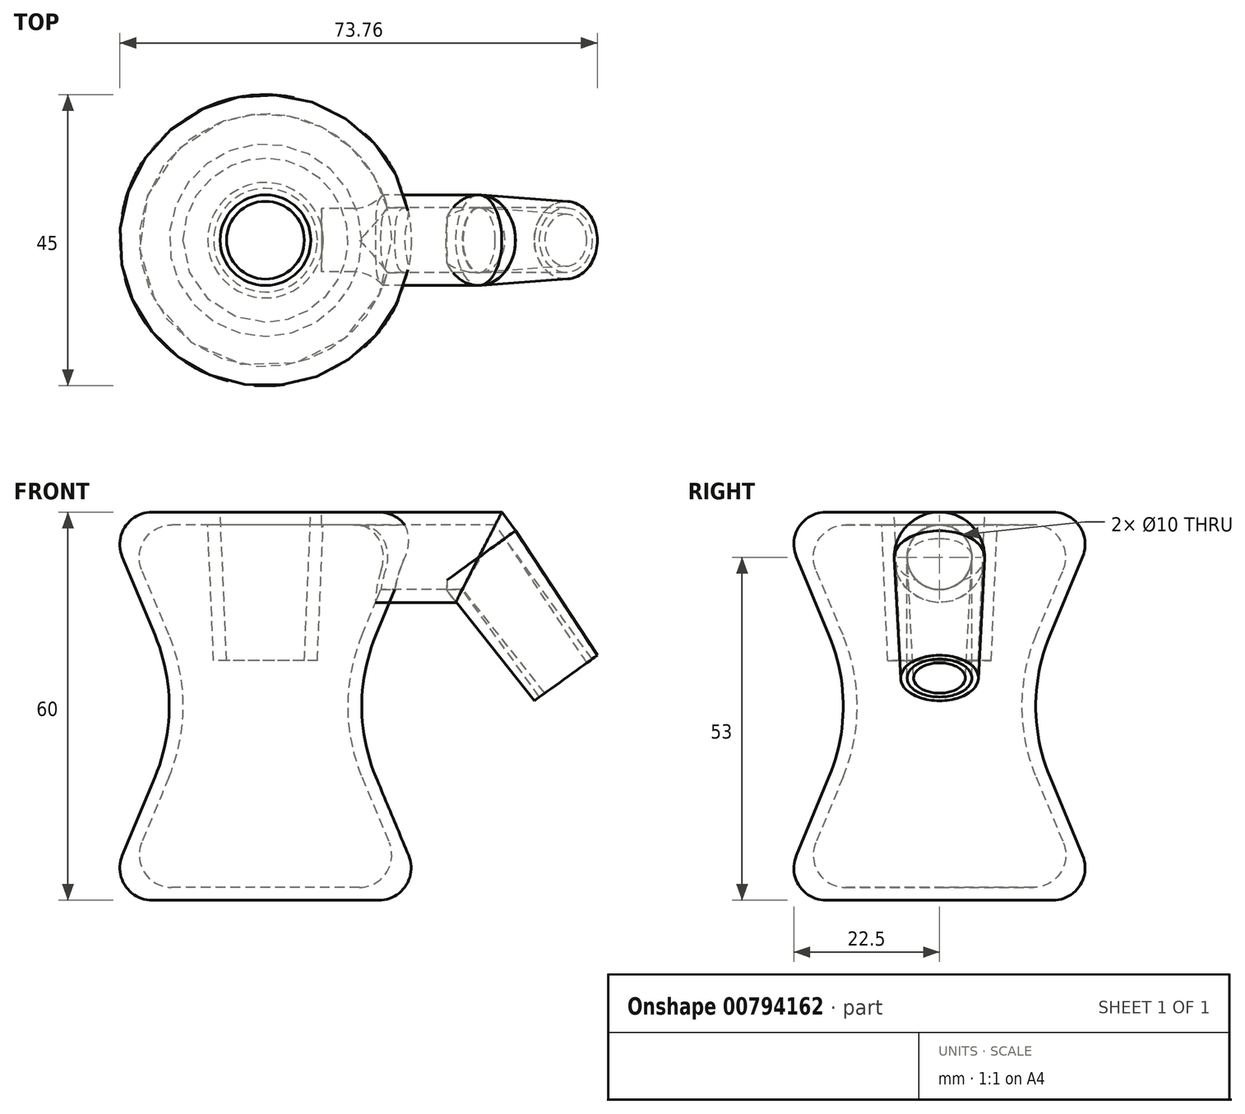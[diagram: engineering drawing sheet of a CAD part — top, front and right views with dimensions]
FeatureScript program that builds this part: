
annotation { "Feature Type Name" : "Feature", "Feature Type Description" : "" }
export const myFeature = defineFeature(function(context is Context, id is Id, definition is map)
    precondition{}
    {
        {
            var Q0;
            Q0=qCreatedBy(makeId("Front.planeOp"),FACE);
            var sketch = newSketch(context, id + "F0", { "sketchPlane" : qUnion([Q0])});
            skLineSegment(sketch, "E0", {"start": v(0, 0) * mm, "end": v(25, 0) * mm});
            skLineSegment(sketch, "E1", {"start": v(25, 0) * mm, "end": v(12.5, 30) * mm});
            skLineSegment(sketch, "E2", {"start": v(12.5, 30) * mm, "end": v(0, 30) * mm});
            skLineSegment(sketch, "E3.MirrorCS", {"start": v(25, 60) * mm, "end": v(12.5, 30) * mm});
            skLineSegment(sketch, "E4.MirrorCS", {"start": v(0, 60) * mm, "end": v(25, 60) * mm});
            skLineSegment(sketch, "E5.0", {"start": v(0, 58) * mm, "end": v(22, 58) * mm});
            skLineSegment(sketch, "E5.1", {"start": v(22, 58) * mm, "end": v(10.33, 30) * mm});
            skLineSegment(sketch, "E5.2", {"start": v(22, 2) * mm, "end": v(10.33, 30) * mm});
            skLineSegment(sketch, "E5.3", {"start": v(0, 2) * mm, "end": v(22, 2) * mm});
            skLineSegment(sketch, "E6", {"start": v(7, 60) * mm, "end": v(6, 37.02) * mm});
            skLineSegment(sketch, "E7", {"start": v(6, 37.02) * mm, "end": v(0, 37.02) * mm});
            skLineSegment(sketch, "E8", {"start": v(9, 60) * mm, "end": v(8, 37.02) * mm});
            skLineSegment(sketch, "E9", {"start": v(6, 37.02) * mm, "end": v(8, 37.02) * mm});
            skLineSegment(sketch, "E10", {"start": v(0, 60) * mm, "end": v(0, 0) * mm});
            skLineSegment(sketch, "E11", {"start": v(8.7, 53) * mm, "end": v(32.94, 53) * mm});
            skLineSegment(sketch, "E12", {"start": v(32.94, 53) * mm, "end": v(46.4, 34.35) * mm});
            skLineSegment(sketch, "E13", {"start": v(32.94, 53) * mm, "end": v(38.61, 57.1) * mm});
            skLineSegment(sketch, "E14", {"start": v(46.4, 34.35) * mm, "end": v(51.26, 37.86) * mm});
            skLineSegment(sketch, "E15", {"start": v(51.26, 37.86) * mm, "end": v(38.61, 57.1) * mm});
            skLineSegment(sketch, "E16", {"start": v(37, 55.92) * mm, "end": v(49.64, 36.69) * mm});
            skLineSegment(sketch, "E17", {"start": v(38.61, 57.1) * mm, "end": v(36.52, 60) * mm});
            skLineSegment(sketch, "E18", {"start": v(37, 55.92) * mm, "end": v(34.31, 60) * mm});
            skLineSegment(sketch, "E19", {"start": v(36.52, 60) * mm, "end": v(25, 60) * mm});
            skLineSegment(sketch, "E20", {"start": v(22, 58) * mm, "end": v(37.96, 58) * mm});
            skLineSegment(sketch, "E21", {"start": v(38.61, 57.1) * mm, "end": v(47.49, 63.5) * mm});
            skLineSegment(sketch, "E22", {"start": v(47.49, 63.5) * mm, "end": v(62.15, 37) * mm});
            skLineSegment(sketch, "E23", {"start": v(62.15, 37) * mm, "end": v(51.26, 37.86) * mm});
            skLineSegment(sketch, "E24", {"start": v(38.61, 57.1) * mm, "end": v(52.57, 37.76) * mm});
            skSolve(sketch);
        }
        {
            var Q0;
            {var subQ3=sQuery(id+"F0.wireOp",EDGE,"E0");Q0=makeQuery(id+"F0.imprint","IMPRINT",FACE,{"disambiguationData":[TD([[makeQuery(id+"F0.imprint","IMPRINT",EDGE,{"derivedFrom":subQ3}),1.0]])]});}
            var Q1;
            {var subQ0=sQuery(id+"F0.wireOp",EDGE,"EiZz0BkX-OVOf-3Axu-Wc4k-g7Euzk9zG0Uk");var subQ3=sQuery(id+"F0.wireOp",EDGE,"E5.1");var subQ5=makeQuery(id+"F0.imprint","INTERSECT",VERTEX,{"derivedFrom":[subQ3,subQ0]});Q1=makeQuery(id+"F0.imprint","IMPRINT",FACE,{"disambiguationData":[TD([[makeQuery(id+"F0.imprint","IMPRINT",EDGE,{"disambiguationData":[TD([[subQ5,-1.0]])],"derivedFrom":subQ3}),1.0]])]});}
            var Q2;
            {var subQ8=sQuery(id+"F0.wireOp",EDGE,"E3.MirrorCS");Q2=makeQuery(id+"F0.imprint","IMPRINT",FACE,{"disambiguationData":[TD([[makeQuery(id+"F0.imprint","IMPRINT",EDGE,{"derivedFrom":subQ8}),-1.0]])]});}
            var Q3;
            {var subQ0=sQuery(id+"F0.wireOp",EDGE,"E8");var subQ1=sQuery(id+"F0.wireOp",EDGE,"E4.MirrorCS");var subQ2=makeQuery(id+"F0.imprint","INTERSECT",VERTEX,{"derivedFrom":[subQ1,subQ0]});Q3=makeQuery(id+"F0.imprint","IMPRINT",FACE,{"disambiguationData":[TD([[makeQuery(id+"F0.imprint","IMPRINT",EDGE,{"disambiguationData":[TD([[subQ2,-1.0]])],"derivedFrom":subQ0}),1.0]])]});}
            var Q4;
            {var subQ0=sQuery(id+"F0.wireOp",EDGE,"E6");var subQ1=sQuery(id+"F0.wireOp",EDGE,"E4.MirrorCS");var subQ2=makeQuery(id+"F0.imprint","INTERSECT",VERTEX,{"derivedFrom":[subQ1,subQ0]});Q4=makeQuery(id+"F0.imprint","IMPRINT",FACE,{"disambiguationData":[TD([[makeQuery(id+"F0.imprint","IMPRINT",EDGE,{"disambiguationData":[TD([[subQ2,-1.0]])],"derivedFrom":subQ1}),-1.0]])]});}
            var Q5;
            {var subQ0=sQuery(id+"F0.wireOp",EDGE,"E9");Q5=makeQuery(id+"F0.imprint","IMPRINT",FACE,{"disambiguationData":[TD([[makeQuery(id+"F0.imprint","IMPRINT",EDGE,{"derivedFrom":subQ0}),1.0]])]});}
            var Q6;
            Q6=sQuery(id+"F0.wireOp",EDGE,"E10");
            revolve(context, id + "F1", {"surfaceOperationType" : NewSurfaceOperationType.NEW, "entities" : qUnion([Q0, Q1, Q2, Q3, Q4, Q5]), "axis" : qUnion([Q6]), "revolveType" : RevolveType.FULL});
        }
        {
            var Q0;
            {var subQ0=sQuery(id+"F0.wireOp",EDGE,"E15");Q0=makeQuery(id+"F0.imprint","IMPRINT",FACE,{"disambiguationData":[TD([[makeQuery(id+"F0.imprint","IMPRINT",EDGE,{"derivedFrom":subQ0}),1.0]])]});}
            var Q1;
            Q1=sQuery(id+"F0.wireOp",EDGE,"E12");
            revolve(context, id + "F2", {"surfaceOperationType" : NewSurfaceOperationType.NEW, "entities" : qUnion([Q0]), "axis" : qUnion([Q1]), "revolveType" : RevolveType.FULL});
        }
        {
            var Q0;
            Q0=sQuery(id+"F0.wireOp",VERTEX,"E12.start");
            var Q1;
            Q1=sQuery(id+"F0.wireOp",EDGE,"E11");
            cPlane(context, id + "F3", {"entities" : qUnion([Q0, Q1]), "cplaneType" : CPlaneType.CURVE_POINT, "offset" : 25 * mm, "width" : 150 * mm, "height" : 150 * mm});
        }
        {
            var Q0;
            Q0=qCreatedBy(id+"F3.planeOp",FACE);
            var sketch = newSketch(context, id + "F4", { "sketchPlane" : qUnion([Q0])});
            skPoint(sketch, "E25.0", {"position": v(0, 53) * mm});
            skCircle(sketch, "E26", {"center": v(0, 53) * mm, "radius": 7 * mm});
            skCircle(sketch, "E27", {"center": v(0, 53) * mm, "radius": 5 * mm});
            skSolve(sketch);
        }
        {
            var Q0;
            Q0=makeQuery(id+"F4.imprint","IMPRINT",FACE,{"disambiguationData":[TD([[makeQuery(id+"F4.imprint","IMPRINT",EDGE,{"derivedFrom":sQuery(id+"F4.wireOp",EDGE,"E26")}),1.0]])]});
            var Q1;
            Q1=sQuery(id+"F0.wireOp",EDGE,"E11");
            var Q2;
            Q2=sQuery(id+"F0.wireOp",EDGE,"E12");
            sweep(context, id + "F5", {"profiles" : qUnion([Q0]), "path" : qUnion([Q1, Q2])});
        }
        {
            var Q0;
            Q0=makeQuery(id+"F0.imprint","IMPRINT",FACE,{"disambiguationData":[TD([[makeQuery(id+"F0.imprint","IMPRINT",EDGE,{"derivedFrom":sQuery(id+"F0.wireOp",EDGE,"E15")}),-1.0]])]});
            var Q1;
            Q1=sQuery(id+"F0.wireOp",EDGE,"E12");
            revolve(context, id + "F6", {"operationType" : NewBodyOperationType.REMOVE, "surfaceOperationType" : NewSurfaceOperationType.NEW, "entities" : qUnion([Q0]), "axis" : qUnion([Q1]), "revolveType" : RevolveType.FULL, "oppositeDirection" : true});
        }
        {
            var Q0;
            Q0=makeQuery(id+"F1.opRevolve","SWEPT_EDGE",EDGE,{"disambiguationData":[OSD([sQuery(id+"F0.wireOp",EDGE,"E1"),sQuery(id+"F0.wireOp",EDGE,"E2"),sQuery(id+"F0.wireOp",EDGE,"E3.MirrorCS")])]});
            var Q1;
            Q1=makeQuery(id+"F1.opRevolve","SWEPT_EDGE",EDGE,{"disambiguationData":[OSD([sQuery(id+"F0.wireOp",EDGE,"E2"),sQuery(id+"F0.wireOp",EDGE,"E5.1"),sQuery(id+"F0.wireOp",EDGE,"E5.2")])]});
            fillet(context, id + "F7", {"entities" : qUnion([Q0, Q1]), "radius" : 28.48 * mm, "tangentPropagation" : true, "allowEdgeOverflow" : false});
        }
        {
            var Q0;
            Q0=makeQuery(id+"F1.opRevolve","SWEPT_EDGE",EDGE,{"disambiguationData":[OSD([sQuery(id+"F0.wireOp",EDGE,"E5.0"),sQuery(id+"F0.wireOp",EDGE,"E5.1"),sQuery(id+"F0.wireOp",EDGE,"E20")])]});
            var Q1;
            Q1=makeQuery(id+"F1.opRevolve","SWEPT_EDGE",EDGE,{"disambiguationData":[OSD([sQuery(id+"F0.wireOp",EDGE,"E3.MirrorCS"),sQuery(id+"F0.wireOp",EDGE,"E4.MirrorCS"),sQuery(id+"F0.wireOp",EDGE,"E19")])]});
            var Q2;
            Q2=makeQuery(id+"F1.opRevolve","SWEPT_EDGE",EDGE,{"disambiguationData":[OSD([sQuery(id+"F0.wireOp",EDGE,"E5.2"),sQuery(id+"F0.wireOp",EDGE,"E5.3")])]});
            var Q3;
            Q3=makeQuery(id+"F1.opRevolve","SWEPT_EDGE",EDGE,{"disambiguationData":[OSD([sQuery(id+"F0.wireOp",EDGE,"E0"),sQuery(id+"F0.wireOp",EDGE,"E1")])]});
            fillet(context, id + "F8", {"entities" : qUnion([Q0, Q1, Q2, Q3]), "radius" : 5 * mm, "tangentPropagation" : true, "allowEdgeOverflow" : false});
        }
        {
            var Q0;
            Q0=qCreatedBy(makeId("Front.planeOp"),FACE);
            var sketch = newSketch(context, id + "F9", { "sketchPlane" : qUnion([Q0])});
            skArc(sketch, "E28", {"start": v(-17.06, 19.04) * mm, "mid": v(-14.87, 30) * mm, "end": v(-17.06, 40.96) * mm});
            skArc(sketch, "E29", {"start": v(17.06, 40.96) * mm, "mid": v(14.87, 30) * mm, "end": v(17.06, 19.04) * mm});
            skLineSegment(sketch, "E30", {"start": v(22.12, 53.08) * mm, "end": v(17.06, 40.96) * mm});
            skLineSegment(sketch, "E31", {"start": v(-17.06, 40.96) * mm, "end": v(-22.12, 53.08) * mm});
            skLineSegment(sketch, "E32", {"start": v(-17.5, 60) * mm, "end": v(17.5, 60) * mm});
            skArc(sketch, "E33", {"start": v(-17.5, 60) * mm, "mid": v(-21.66, 57.77) * mm, "end": v(-22.12, 53.08) * mm});
            skArc(sketch, "E34", {"start": v(22.12, 53.08) * mm, "mid": v(21.66, 57.77) * mm, "end": v(17.5, 60) * mm});
            skLineSegment(sketch, "E35.0", {"start": v(-19.12, 51.08) * mm, "end": v(19.12, 51.08) * mm});
            skArc(sketch, "E36", {"start": v(14.9, 40.96) * mm, "mid": v(12.7, 30) * mm, "end": v(14.9, 19.04) * mm});
            skArc(sketch, "E37", {"start": v(-14.9, 19.04) * mm, "mid": v(-12.7, 30) * mm, "end": v(-14.9, 40.96) * mm});
            skLineSegment(sketch, "E38", {"start": v(19.12, 51.08) * mm, "end": v(14.9, 40.96) * mm});
            skLineSegment(sketch, "E39", {"start": v(-14.9, 40.96) * mm, "end": v(-19.12, 51.08) * mm});
            skLineSegment(sketch, "E40", {"start": v(-14.5, 58) * mm, "end": v(14.5, 58) * mm});
            skArc(sketch, "E41", {"start": v(-14.5, 58) * mm, "mid": v(-18.66, 55.77) * mm, "end": v(-19.12, 51.08) * mm});
            skArc(sketch, "E42", {"start": v(19.12, 51.08) * mm, "mid": v(18.66, 55.77) * mm, "end": v(14.5, 58) * mm});
            skLineSegment(sketch, "E43.0.0", {"start": v(8, 37.02) * mm, "end": v(6, 37.02) * mm});
            skLineSegment(sketch, "E43.0.1", {"start": v(6, 37.02) * mm, "end": v(0, 37.02) * mm});
            skLineSegment(sketch, "E43.0.2", {"start": v(0, 37.02) * mm, "end": v(0, 30) * mm});
            skLineSegment(sketch, "E43.0.3", {"start": v(0, 30) * mm, "end": v(10.33, 30) * mm});
            skLineSegment(sketch, "E43.0.4", {"start": v(10.33, 30) * mm, "end": v(19.92, 53) * mm});
            skLineSegment(sketch, "E43.0.5", {"start": v(19.92, 53) * mm, "end": v(8.7, 53) * mm});
            skLineSegment(sketch, "E43.0.6", {"start": v(8.7, 53) * mm, "end": v(8, 37.02) * mm});
            skLineSegment(sketch, "E44.0", {"start": v(9, 60) * mm, "end": v(8, 37.02) * mm});
            skSolve(sketch);
        }
        {
            var Q0;
            {var subQ1=sQuery(id+"F9.wireOp",EDGE,"E38");Q0=makeQuery(id+"F9.imprint","IMPRINT",FACE,{"disambiguationData":[TD([[makeQuery(id+"F9.imprint","IMPRINT",EDGE,{"derivedFrom":subQ1}),-1.0]])]});}
            var Q1;
            {var subQ0=sQuery(id+"F9.wireOp",EDGE,"E42");var subQ5=sQuery(id+"F9.wireOp",EDGE,"E43.0.5");var subQ6=makeQuery(id+"F9.imprint","INTERSECT",VERTEX,{"derivedFrom":[subQ0,subQ5]});Q1=makeQuery(id+"F9.imprint","IMPRINT",FACE,{"disambiguationData":[TD([[makeQuery(id+"F9.imprint","IMPRINT",EDGE,{"disambiguationData":[TD([[subQ6,-1.0]])],"derivedFrom":subQ5}),1.0]])]});}
            var Q2;
            {var subQ0=sQuery(id+"F9.wireOp",EDGE,"E42");var subQ1=sQuery(id+"F9.wireOp",EDGE,"E40");var subQ2=makeQuery(id+"F9.imprint","INTERSECT",VERTEX,{"derivedFrom":[subQ1,subQ0]});Q2=makeQuery(id+"F9.imprint","IMPRINT",FACE,{"disambiguationData":[TD([[makeQuery(id+"F9.imprint","IMPRINT",EDGE,{"disambiguationData":[TD([[subQ2,1.0]])],"derivedFrom":subQ1}),-1.0]])]});}
            var Q3;
            Q3=sQuery(id+"F0.wireOp",EDGE,"E10");
            revolve(context, id + "F10", {"operationType" : NewBodyOperationType.REMOVE, "surfaceOperationType" : NewSurfaceOperationType.NEW, "entities" : qUnion([Q0, Q1, Q2]), "axis" : qUnion([Q3]), "revolveType" : RevolveType.FULL, "oppositeDirection" : true});
        }
        {
            var Q0;
            Q0=sQuery(id+"F0.wireOp",VERTEX,"E13.start");
            var Q1;
            Q1=sQuery(id+"F0.wireOp",EDGE,"E11");
            cPlane(context, id + "F11", {"entities" : qUnion([Q0, Q1]), "cplaneType" : CPlaneType.CURVE_POINT, "offset" : 25 * mm, "width" : 150 * mm, "height" : 150 * mm});
        }
        {
            var Q0;
            Q0=qCreatedBy(id+"F11.planeOp",FACE);
            var sketch = newSketch(context, id + "F12", { "sketchPlane" : qUnion([Q0])});
            skPoint(sketch, "E45.0", {"position": v(0, 53) * mm});
            skCircle(sketch, "E46", {"center": v(0, 53) * mm, "radius": 5 * mm});
            skSolve(sketch);
        }
        {
            var Q0;
            Q0=makeQuery(id+"F12.imprint","IMPRINT",FACE,{"disambiguationData":[TD([[makeQuery(id+"F12.imprint","IMPRINT",EDGE,{"derivedFrom":sQuery(id+"F12.wireOp",EDGE,"E46")}),1.0]])]});
            extrude(context, id + "F13", {"entities" : qUnion([Q0]), "operationType" : NewBodyOperationType.REMOVE, "oppositeDirection" : true, "depth" : 19.44 * mm, "offsetDistance" : 25 * mm});
        }
    });
